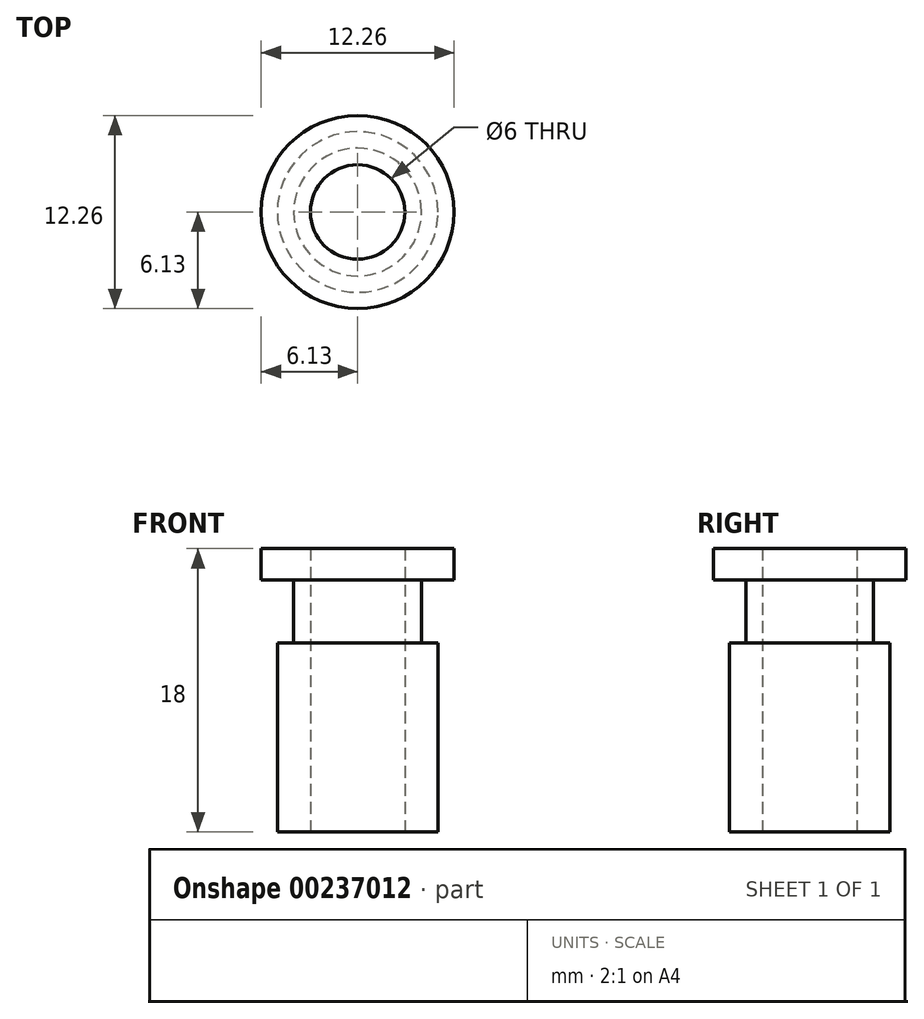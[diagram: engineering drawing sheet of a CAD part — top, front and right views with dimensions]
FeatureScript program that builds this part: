
annotation { "Feature Type Name" : "Feature", "Feature Type Description" : "" }
export const myFeature = defineFeature(function(context is Context, id is Id, definition is map)
    precondition{}
    {
        {
            var Q0;
            Q0=qCreatedBy(makeId("Front.planeOp"),FACE);
            var sketch = newSketch(context, id + "F0", { "sketchPlane" : qUnion([Q0])});
            skLineSegment(sketch, "E0", {"start": v(0, 0) * mm, "end": v(0, 4.75) * mm, "construction": true});
            skLineSegment(sketch, "E1", {"start": v(3, 18) * mm, "end": v(3, 0) * mm});
            skLineSegment(sketch, "E2", {"start": v(3, 0) * mm, "end": v(5.1, 0) * mm});
            skLineSegment(sketch, "E3", {"start": v(5.1, 0) * mm, "end": v(5.1, 12) * mm});
            skLineSegment(sketch, "E4", {"start": v(5.1, 12) * mm, "end": v(4.06, 12) * mm});
            skLineSegment(sketch, "E5", {"start": v(4.06, 12) * mm, "end": v(4.06, 16) * mm});
            skLineSegment(sketch, "E6", {"start": v(4.06, 16) * mm, "end": v(6.13, 16) * mm});
            skLineSegment(sketch, "E7", {"start": v(6.13, 16) * mm, "end": v(6.13, 18) * mm});
            skLineSegment(sketch, "E8", {"start": v(6.13, 18) * mm, "end": v(3, 18) * mm});
            skSolve(sketch);
        }
        {
            var Q0;
            Q0=makeQuery(id+"F0.imprint","IMPRINT",FACE,{"disambiguationData":[TD([[makeQuery(id+"F0.imprint","IMPRINT",EDGE,{"derivedFrom":sQuery(id+"F0.wireOp",EDGE,"E1")}),1.0]])]});
            var Q1;
            Q1=sQuery(id+"F0.wireOp",EDGE,"E0");
            revolve(context, id + "F1", {"entities" : qUnion([Q0]), "axis" : qUnion([Q1]), "revolveType" : RevolveType.FULL});
        }
    });
